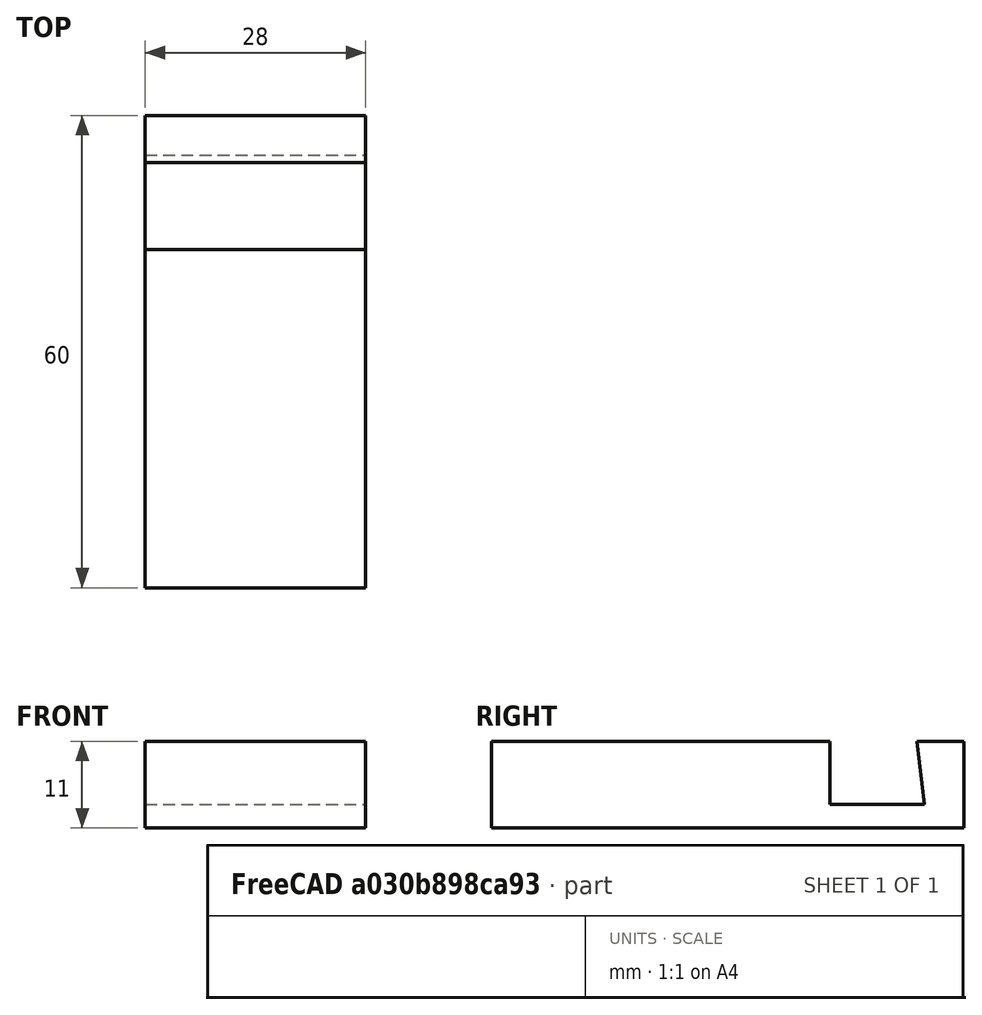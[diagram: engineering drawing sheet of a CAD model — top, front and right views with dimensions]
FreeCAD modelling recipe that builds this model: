
FCSTD DOCUMENT  (FreeCAD 0.20R29177 +233 (Git))
Label: Soporte-para-movil
License: Creative Commons Attribution-ShareAlike
LicenseURL: http://creativecommons.org/licenses/by-sa/4.0/
objects: Sketcher::SketchObject×1, Part::Extrusion×1
note: 2 computed .brp shape members not serialized (recipe doc carries the construction recipe); baked Part::Feature solids carry a one-line shape summary decoded from their .brp

FEATURE [Sketcher::SketchObject] Sketch
  FullyConstrained = true
  Placement = pos=(0,0,0) rot=(0.57735,0.57735,0.57735;2.0944rad)
  sketch-geometry (8):
    g0: LineSegment StartX=0 StartY=11 StartZ=0 EndX=0 EndY=0 EndZ=0
    g1: LineSegment StartX=0 StartY=0 StartZ=0 EndX=60 EndY=0 EndZ=0
    g2: LineSegment StartX=60 StartY=11 StartZ=0 EndX=60 EndY=0 EndZ=0
    g3: LineSegment StartX=54 StartY=11 StartZ=0 EndX=60 EndY=11 EndZ=0
    g4: LineSegment StartX=0 StartY=11 StartZ=0 EndX=43 EndY=11 EndZ=0
    g5: LineSegment StartX=43 StartY=3 StartZ=0 EndX=55 EndY=3 EndZ=0
    g6: LineSegment StartX=43 StartY=11 StartZ=0 EndX=43 EndY=3 EndZ=0
    g7: LineSegment StartX=54 StartY=11 StartZ=0 EndX=55 EndY=3 EndZ=0
  constraints (23):
    c: Horizontal(g1)
    c: Vertical(g0)
    c: Coincident(g0,g1)
    c: Coincident(g0,g-1)
    c: DistanceX(g1,g1) = 60
    c: DistanceY(g0,g0) = 11
    c: Equal(g2,g0)
    c: Vertical(g2)
    c: Coincident(g2,g1)
    c: Horizontal(g3)
    c: Horizontal(g4)
    c: Coincident(g4,g0)
    c: Coincident(g3,g2)
    c: Distance(g4,g3) = 11
    c: Distance(g3,g2) = 6
    c: Horizontal(g5)
    c: DistanceX(g5,g5) = 12
    c: Vertical(g6)
    c: Coincident(g6,g4)
    c: Distance(g6,g1) = 3
    c: Coincident(g5,g6)
    c: Coincident(g7,g3)
    c: Coincident(g7,g5)
FEATURE [Part::Extrusion] Extrude
  Base = -> Sketch
  Dir = (1,0,0)
  DirMode = 2
  FaceMakerClass = Part::FaceMakerBullseye
  LengthFwd = 28
  LengthRev = 0
  Solid = true
  Symmetric = false
